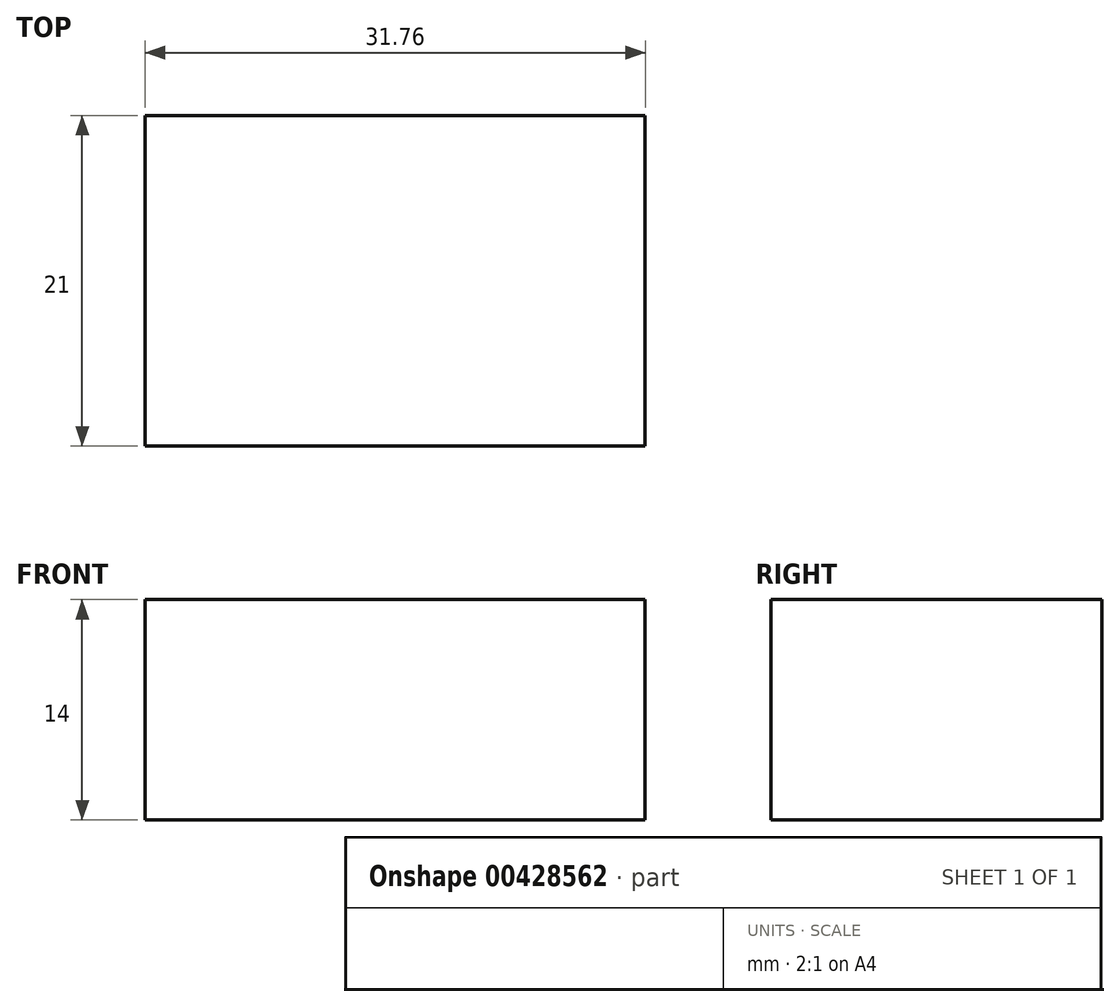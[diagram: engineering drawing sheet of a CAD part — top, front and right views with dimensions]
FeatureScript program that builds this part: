
annotation { "Feature Type Name" : "Feature", "Feature Type Description" : "" }
export const myFeature = defineFeature(function(context is Context, id is Id, definition is map)
    precondition{}
    {
        {
            var Q0;
            Q0=qCreatedBy(makeId("Top.planeOp"),FACE);
            var sketch = newSketch(context, id + "F0", { "sketchPlane" : qUnion([Q0])});
            skLineSegment(sketch, "E0.bottom", {"start": v(15.87, 10.5) * mm, "end": v(-15.87, 10.5) * mm});
            skLineSegment(sketch, "E0.top", {"start": v(15.87, -10.5) * mm, "end": v(-15.87, -10.5) * mm});
            skLineSegment(sketch, "E0.left", {"start": v(15.87, 10.5) * mm, "end": v(15.87, -10.5) * mm});
            skLineSegment(sketch, "E0.right", {"start": v(-15.87, 10.5) * mm, "end": v(-15.87, -10.5) * mm});
            skPoint(sketch, "E0.middle", {"position": v(0, 0) * mm});
            skSolve(sketch);
        }
        {
            var Q0;
            Q0 = qSketchRegion(id + "F0", true);
            extrude(context, id + "F1", {"entities" : qUnion([Q0]), "depth" : 14 * mm});
        }
    });
